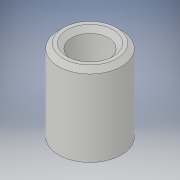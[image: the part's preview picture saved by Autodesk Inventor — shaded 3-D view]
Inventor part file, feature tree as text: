
AUTODESK INVENTOR PART (.ipt)
format: ipt  version: 2018 (Build 220112000, 112)  size: 109,056 bytes
history: native  units: in
note: dims shown in document units (in); Inventor stores cm internally (conversion verified against a paired STEP export)
features: extrude x1, chamfer x1, sketch x1
ambient origin geometry x8: Origin, YZ Plane, XZ Plane, XY Plane, X Axis, Y Axis, Z Axis, Center Point
bodies: Solid1 (feature_tree)
feature tree (3):
  extrude  "Extrusion1"  Depth=0.125in
  chamfer  "Chamfer1"  Distance=0.55in
  sketch  "Sketch1"  dims[d0=0.25in d1=0.425in d2=0.55in d3=0.0in d4=0.0312in d5=0.125in d6=45.0deg]
